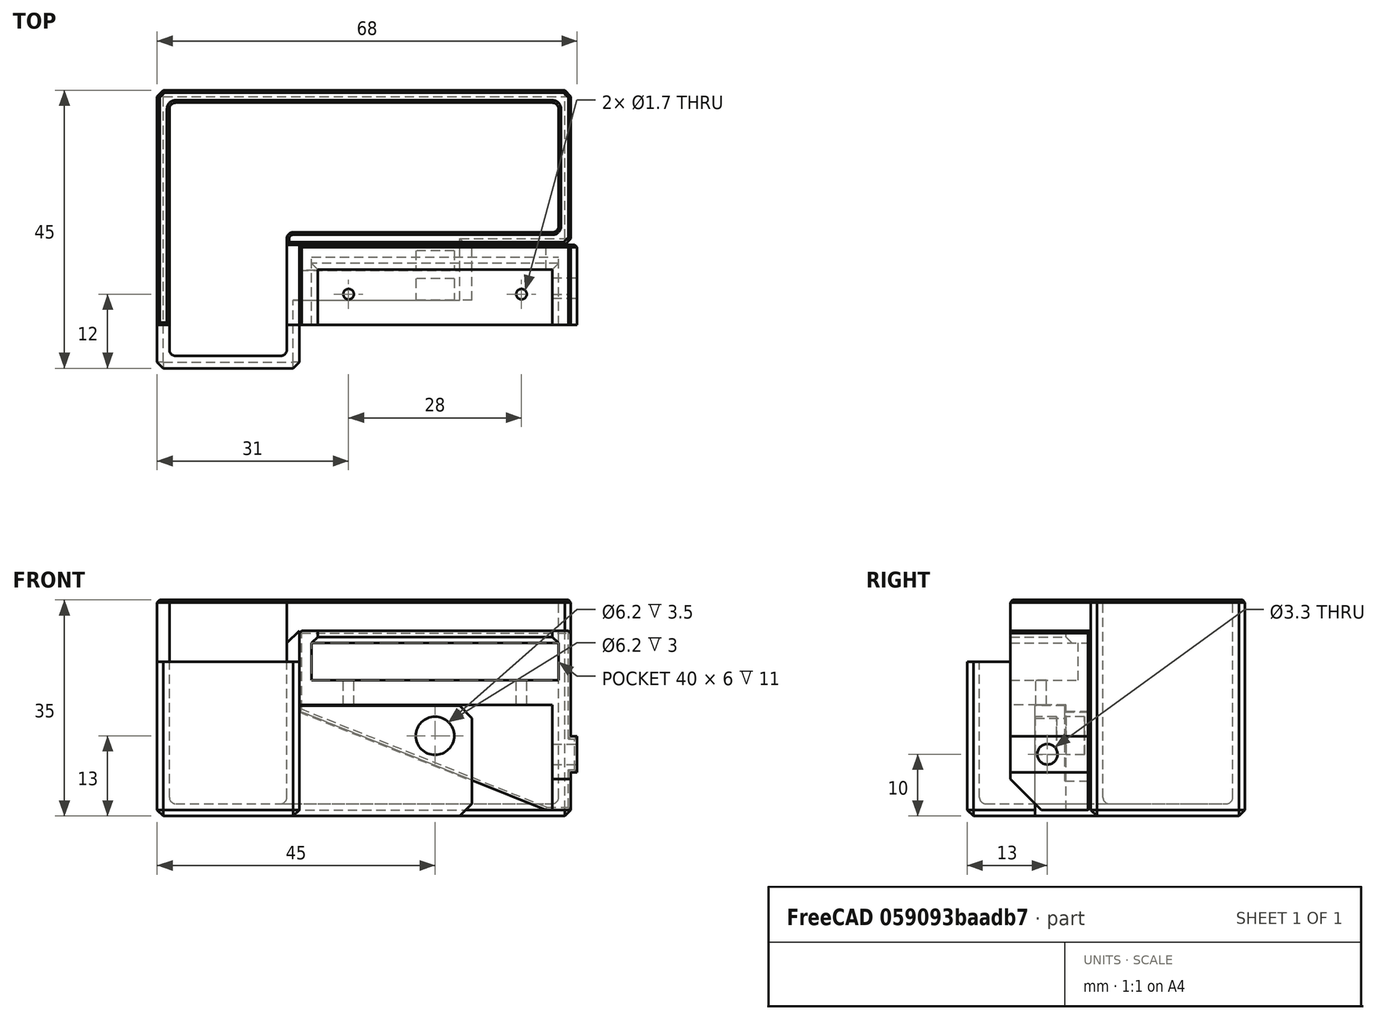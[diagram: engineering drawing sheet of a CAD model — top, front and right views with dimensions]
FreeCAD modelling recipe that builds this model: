
FCSTD DOCUMENT  (FreeCAD 0.19R24291 (Git))
Label: bucket
License: Other
LicenseURL: GPL3
objects: Part::Box×15, Part::Chamfer×11, Part::Cut×10, Part::MultiFuse×7, Part::Cylinder×5, Part::Refine×3, Part::Fillet×1
note: 52 computed .brp shape members not serialized (recipe doc carries the construction recipe); baked Part::Feature solids carry a one-line shape summary decoded from their .brp

FEATURE [Part::Box] Box024  label="Cube023"
  AttacherType = Attacher::AttachEngine3D
  Height = 12
  Length = 44
  Width = 15
FEATURE [Part::Box] Box025  label="Cube024"
  AttacherType = Attacher::AttachEngine3D
  Height = 12
  Length = 38
  Placement = pos=(3,0,4) rot=(0,0,1;0rad)
  Width = 11
FEATURE [Part::Box] Box026  label="Cube025"
  AttacherType = Attacher::AttachEngine3D
  Height = 6
  Length = 40
  Placement = pos=(2,0,4) rot=(0,0,1;0rad)
  Width = 13
FEATURE [Part::Cut] Cut008
  Base = -> Box024
  Tool = -> Box026
FEATURE [Part::Cut] Cut009
  Base = -> Cut008
  Tool = -> Box025
FEATURE [Part::Chamfer] Chamfer010
  Base = -> Cut009
  Edges = 3 edges r=0.99: [Edge27,Edge30,Edge31]
FEATURE [Part::Box] Box027  label="Cube026"
  AttacherType = Attacher::AttachEngine3D
  Height = 19
  Length = 48
  Placement = pos=(0,-8,0) rot=(0,0,1;0rad)
  Width = 10
FEATURE [Part::Cut] Cut010
  Base = -> Chamfer010
  Placement = pos=(-44,0,18) rot=(0,0,1;0rad)
  Tool = -> Box027
FEATURE [Part::Box] Box028  label="Cube027"
  AttacherType = Attacher::AttachEngine3D
  Height = 18
  Length = 3
  Placement = pos=(-3,2,1) rot=(0,0,1;0rad)
  Width = 13
FEATURE [Part::Box] Box029  label="Cube028"
  AttacherType = Attacher::AttachEngine3D
  Height = 5.8
  Length = 2
  Placement = pos=(-1,2,7.1) rot=(0,0,1;0rad)
  Width = 13
FEATURE [Part::Cylinder] Cylinder004
  Angle = 360
  AttacherType = Attacher::AttachEngine3D
  Height = 10
  Placement = pos=(-5,8,10) rot=(0,1,0;1.5708rad)
  Radius = 1.65
FEATURE [Part::Box] Box030  label="Cube029"
  AttacherType = Attacher::AttachEngine3D
  Height = 18
  Length = 42
  Placement = pos=(-44,11,1) rot=(0,0,1;0rad)
  Width = 4
FEATURE [Part::MultiFuse] Fusion001008008002
  Shapes = -> [Box028,Box029,Box030]
FEATURE [Part::Cut] Cut011
  Base = -> Fusion001008008002
  Tool = -> Cylinder004
FEATURE [Part::Chamfer] Chamfer011
  Base = -> Cut011
  Edges = 1 edges: [Edge39 r1=40 r2=16]
FEATURE [Part::Chamfer] Chamfer012
  Base = -> Chamfer011
  Edges = 1 edges r=5: [Edge33]
FEATURE [Part::Cylinder] Cylinder006
  Angle = 360
  AttacherType = Attacher::AttachEngine3D
  Height = 10
  Placement = pos=(-22,9.5,13) rot=(1,0,0;1.5708rad)
  Radius = 3.1
FEATURE [Part::Cylinder] Cylinder007
  Angle = 360
  AttacherType = Attacher::AttachEngine3D
  Height = 10
  Placement = pos=(-22,14,13) rot=(1,0,0;1.5708rad)
  Radius = 3.1
FEATURE [Part::Cylinder] Cylinder008
  Angle = 360
  AttacherType = Attacher::AttachEngine3D
  Height = 10
  Placement = pos=(-8,7,14) rot=(0,0,1;0rad)
  Radius = 0.85
FEATURE [Part::MultiFuse] Fusion001008008003
  Shapes = -> [Chamfer012,Cut010]
FEATURE [Part::Refine] Fusion001008008003001
  Source = -> Fusion001008008003
FEATURE [Part::Chamfer] Chamfer013
  Base = -> Fusion001008008003001
  Edges = 11 edges r=0.4: [Edge20,Edge23,Edge27,Edge29,Edge31,Edge47,Edge51,Edge52,Edge71,Edge72,Edge73]
FEATURE [Part::Cut] Cut012
  Base = -> Chamfer013
  Tool = -> Cylinder007
FEATURE [Part::Cylinder] Cylinder009
  Angle = 360
  AttacherType = Attacher::AttachEngine3D
  Height = 10
  Placement = pos=(-36,7,14) rot=(0,0,1;0rad)
  Radius = 0.85
FEATURE [Part::MultiFuse] Fusion001008008003002
  Shapes = -> [Cylinder009,Cylinder008]
FEATURE [Part::Cut] Cut013
  Base = -> Cut012
  Tool = -> Fusion001008008003002
FEATURE [Part::Box] Box031  label="Cube030"
  AttacherType = Attacher::AttachEngine3D
  Height = 10
  Length = 10
  Placement = pos=(-51,1,30) rot=(0,0,1;0rad)
  Width = 14
FEATURE [Part::Chamfer] Chamfer
  Base = -> Box031
  Edges = 1 edges r=2: [Edge8]
  Placement = pos=(-3,0,-2) rot=(0,0,1;0rad)
FEATURE [Part::Box] Box  label="Cube"
  AttacherType = Attacher::AttachEngine3D
  Height = 35
  Length = 23
  Placement = pos=(-67,-5,0) rot=(0,0,1;0rad)
  Width = 45
FEATURE [Part::Box] Box032  label="Cube031"
  AttacherType = Attacher::AttachEngine3D
  Height = 35
  Length = 44
  Placement = pos=(-44,15,0) rot=(0,0,1;0rad)
  Width = 25
FEATURE [Part::Box] Box033  label="Cube032"
  AttacherType = Attacher::AttachEngine3D
  Height = 35
  Length = 19
  Placement = pos=(-65,-3,2) rot=(0,0,1;0rad)
  Width = 41
FEATURE [Part::Box] Box034  label="Cube033"
  AttacherType = Attacher::AttachEngine3D
  Height = 35
  Length = 44
  Placement = pos=(-46,17,2) rot=(0,0,1;0rad)
  Width = 21
FEATURE [Part::MultiFuse] Fusion
  Shapes = -> [Box033,Box034]
FEATURE [Part::MultiFuse] Fusion001008008003003
  Shapes = -> [Box,Box032]
FEATURE [Part::Refine] Fusion001008008003004
  Source = -> Fusion
FEATURE [Part::Refine] Fusion001008008003003001
  Source = -> Fusion001008008003003
FEATURE [Part::Fillet] Fillet
  Base = -> Fusion001008008003004
  Edges = 12 edges r=1: [Edge1,Edge3,Edge4,Edge5,Edge6,Edge9,Edge10,Edge11,Edge12,Edge15,Edge16,Edge18]
FEATURE [Part::Chamfer] Chamfer014
  Base = -> Fusion001008008003003001
  Edges = 11 edges r=1: [Edge1,Edge3,Edge4,Edge5,Edge6,Edge10,Edge11,Edge12,Edge15,Edge16,Edge18]
FEATURE [Part::Cut] Cut
  Base = -> Chamfer014
  Tool = -> Fillet
FEATURE [Part::Box] Box035  label="Cube034"
  AttacherType = Attacher::AttachEngine3D
  Height = 17.85
  Length = 29
  Placement = pos=(-45,6,0) rot=(0,0,1;0rad)
  Width = 4.85
FEATURE [Part::Box] Box036  label="Cube035"
  AttacherType = Attacher::AttachEngine3D
  Height = 16.85
  Length = 29
  Placement = pos=(-45,10.85,0) rot=(0,0,1;0rad)
  Width = 5.5
FEATURE [Part::Chamfer] Chamfer015
  Base = -> Box036
  Edges = 1 edges: [Edge6 r1=11.15 r2=28]
FEATURE [Part::Chamfer] Chamfer016
  Base = -> Box035
  Edges = 1 edges r=2: [Edge6]
FEATURE [Part::Chamfer] Chamfer017
  Base = -> Chamfer016
  Edges = 1 edges r=2: [Edge2]
FEATURE [Part::Chamfer] Chamfer018
  Base = -> Chamfer015
  Edges = 1 edges r=2: [Edge2]
FEATURE [Part::MultiFuse] Fusion001008008003003002
  Shapes = -> [Chamfer017,Chamfer018]
FEATURE [Part::Cut] Cut014
  Base = -> Fusion001008008003003002
  Tool = -> Cylinder006
FEATURE [Part::MultiFuse] Fusion001008008003003003
  Shapes = -> [Cut,Cut014]
FEATURE [Part::Cut] Cut015
  Base = -> Fusion001008008003003003
  Tool = -> Chamfer
FEATURE [Part::Box] Box037  label="Cube036"
  AttacherType = Attacher::AttachEngine3D
  Height = 10
  Length = 29
  Placement = pos=(-69,-8,25) rot=(0,0,1;0rad)
  Width = 10
FEATURE [Part::Cut] Cut016
  Base = -> Cut015
  Tool = -> Box037
FEATURE [Part::Chamfer] Chamfer019
  Base = -> Cut016
  Edges = 18 edges r=0.4: [Edge1,Edge7,Edge8,Edge9,Edge10,Edge11,Edge12,Edge13,Edge14,Edge15,Edge16,Edge17,Edge18,Edge19,Edge20,Edge21,Edge22,Edge23]
